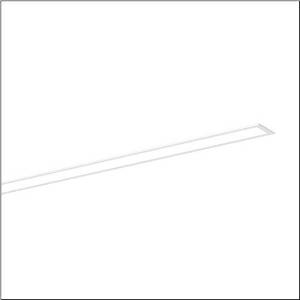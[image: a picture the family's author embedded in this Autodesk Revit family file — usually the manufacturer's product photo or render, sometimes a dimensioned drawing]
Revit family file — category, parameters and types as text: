
# Revit family: silica_21_51mx10dc45wb
name_source: partatom
category: Lighting Fixtures
units: mm (PartAtom-declared; Revit-internal decimal feet)

## family parameters
Cut with Voids When Loaded = No
Host = Face
Light Source = No
Part Type = Normal
Room Calculation Point = No
Round Connector Dimension = Use Diameter
Shared = No

## types (1)
- --- (1 x LED, 6000 lm, 40.1 W, 4000K)
    Apparent Load = 40 VA
    CIE Flux Codes = 48 79 96 100 100
    Color Rendering = 80
    Color Temperature = 4000K
    Default Elevation = 1800 mm
    Description = Silica 21, office luminaire, primary optical cover: cover, of PMMA, opal, light emission: direct distribution, primary light characteristic: symmetric, installation type: recessed, LED, rated luminous flux: 6.000lm, luminous efficacy: 150lm/W, light colour: 840, colour temperature: 4000K, control gear: DALI 2, with terminal, 3+2-pole, max. 2.5mm², mains connection: 220..240V, AC, 50/60Hz, rated input power: 40.1W, luminaire housing, of aluminium, traffic white (RAL 9016), length: 3.028mm, width: 79mm, height: 53mm, protection rating (complete): IP20, insulation class (complete): insulation class I (protective earthing), certification: CE, ENEC, VDE, permissible operating ambient temperature: 0..+35°C, standard: EN 50419, packaging unit: 1 piece
    Height = 0 mm  [stored 0 ft]
    Lamp = 1 x LED
    Lamp Light Flux = 6000 lm
    Lamp Power = 40.1 W
    Lamp count = 1
    Length = 3027 mm
    Luminous efficacy = 150 lm/W
    Manufacturer = Siteco
    ModVariant = No
    Model = 51MX10DC45WB
    Mounting Place = Ceiling
    Mounting Type = Recessed
    Number of Poles = 1
    OnlyDefault = Yes
    Power Factor = 1
    Product Name = Silica 21
    Product group = office luminaire | ceiling recessed
    ProductGroupID = 400
    Protection Class = Protection class I
    Protection Degree = IP 20
    RLX_Detail_Level = 1
    RLX_Emergency_Light_Flux = 0 lm
    RLX_Emergency_Type = 0
    RLX_Emergency_Type_DB = No
    RlxData = <blob elided: 21229 chars, md5=fae747df>
    Socket = socket
    Standby Power = 0 W
    System Light Flux = 6000 lm
    System Power = 40 W
    Type Comments = factory setting: luminous flux: 100 % | dim-lin: 254 | 218 mA
    Type Image = l_1335891.jpg
    URL = http://relux.com
    VarID = @adj_117721
    Voltage = 0 V
    Weight = 0.00 kg
    Width = 79 mm

note: [stored X ft] marks values corroborated as IEEE doubles in the binary element streams (Revit-internal decimal feet)

## geometry (parser evidence)
native form markers: Blend x4, Sweep x11
no freeform markers — native parametric forms only
